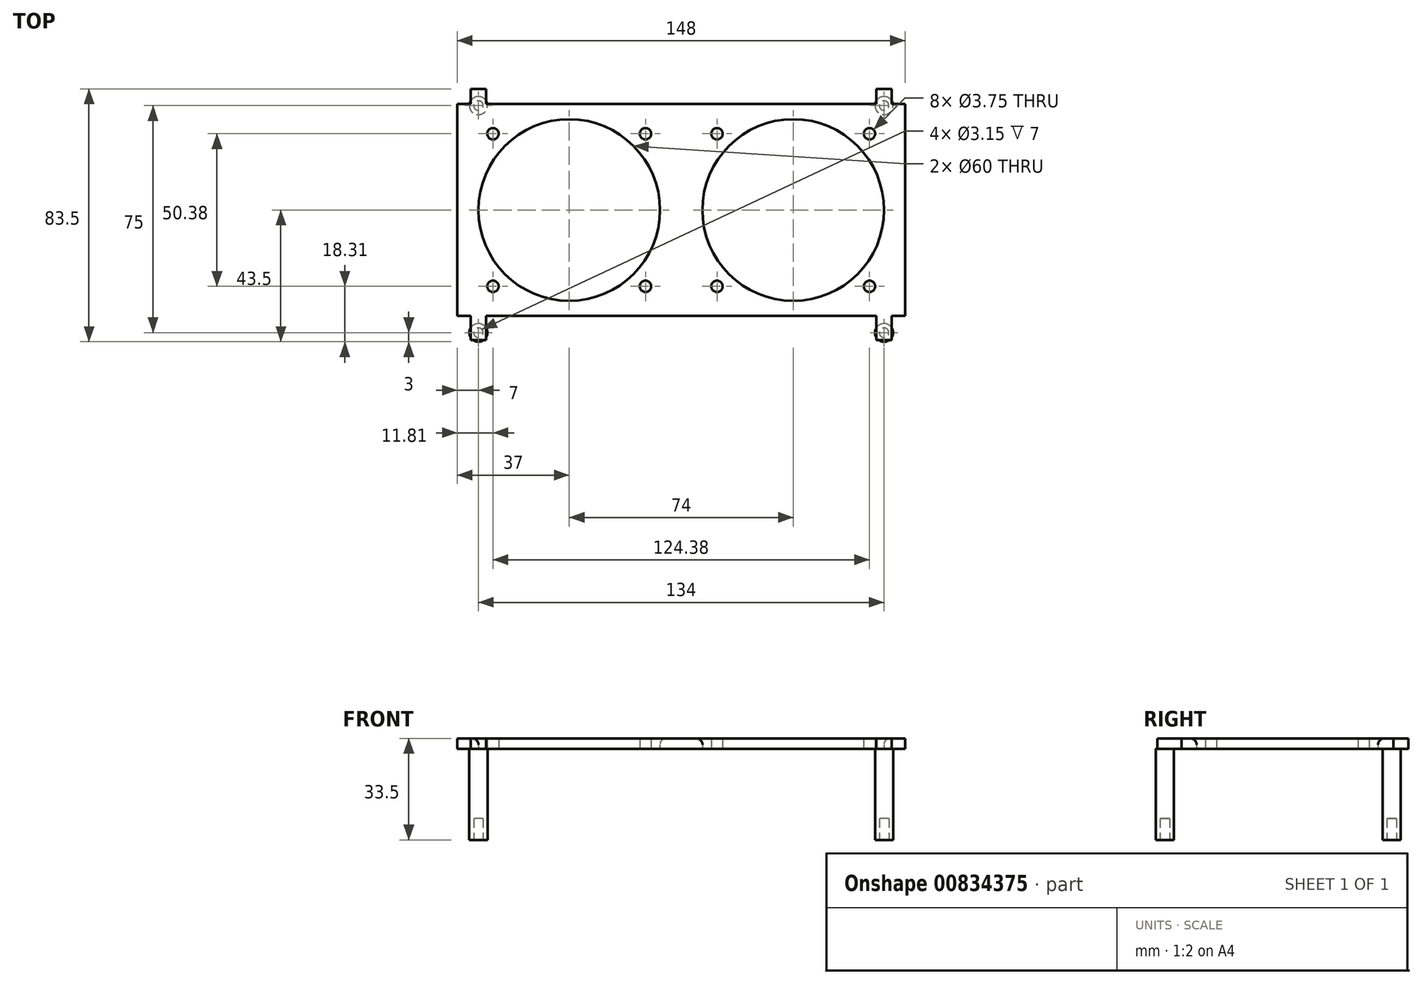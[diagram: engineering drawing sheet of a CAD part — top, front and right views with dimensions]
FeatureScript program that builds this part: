
annotation { "Feature Type Name" : "Feature", "Feature Type Description" : "" }
export const myFeature = defineFeature(function(context is Context, id is Id, definition is map)
    precondition{}
    {
        {
            var Q0;
            Q0=qCreatedBy(makeId("Top.planeOp"),FACE);
            var sketch = newSketch(context, id + "F0", { "sketchPlane" : qUnion([Q0])});
            skLineSegment(sketch, "E0.bottom", {"start": v(74, -35) * mm, "end": v(69.5, -35) * mm});
            skLineSegment(sketch, "E0.top", {"start": v(74, 35) * mm, "end": v(-74, 35) * mm});
            skLineSegment(sketch, "E0.left", {"start": v(74, -35) * mm, "end": v(74, 35) * mm});
            skLineSegment(sketch, "E0.right", {"start": v(-74, -35) * mm, "end": v(-74, 35) * mm});
            skPoint(sketch, "E0.middle", {"position": v(0, 0) * mm});
            skCircle(sketch, "E1", {"center": v(-37, 0) * mm, "radius": 30 * mm});
            skCircle(sketch, "E2", {"center": v(37, 0) * mm, "radius": 30 * mm});
            skLineSegment(sketch, "E3.bottom", {"start": v(-64.5, -43) * mm, "end": v(-69.5, -43) * mm});
            skLineSegment(sketch, "E3.left", {"start": v(-64.5, -43) * mm, "end": v(-64.5, -35) * mm});
            skLineSegment(sketch, "E3.right", {"start": v(-69.5, -43) * mm, "end": v(-69.5, -35) * mm});
            skPoint(sketch, "E3.middle", {"position": v(-67, -39) * mm});
            skLineSegment(sketch, "E4.bottom", {"start": v(69.5, -43) * mm, "end": v(64.5, -43) * mm});
            skLineSegment(sketch, "E4.left", {"start": v(69.5, -43) * mm, "end": v(69.5, -35) * mm});
            skLineSegment(sketch, "E4.right", {"start": v(64.5, -43) * mm, "end": v(64.5, -35) * mm});
            skPoint(sketch, "E4.middle", {"position": v(67, -39) * mm});
            skLineSegment(sketch, "E5.trimOffspring", {"start": v(-69.5, -35) * mm, "end": v(-74, -35) * mm});
            skLineSegment(sketch, "E6.trimOffspring", {"start": v(64.5, -35) * mm, "end": v(-64.5, -35) * mm});
            skLineSegment(sketch, "E7.bottom", {"start": v(-64.5, 35) * mm, "end": v(-69.5, 35) * mm});
            skLineSegment(sketch, "E7.top", {"start": v(-64.5, 40) * mm, "end": v(-69.5, 40) * mm});
            skLineSegment(sketch, "E7.left", {"start": v(-64.5, 35) * mm, "end": v(-64.5, 40) * mm});
            skLineSegment(sketch, "E7.right", {"start": v(-69.5, 35) * mm, "end": v(-69.5, 40) * mm});
            skPoint(sketch, "E7.middle", {"position": v(-67, 37.5) * mm});
            skLineSegment(sketch, "E8.bottom", {"start": v(69.5, 35) * mm, "end": v(64.5, 35) * mm});
            skLineSegment(sketch, "E8.top", {"start": v(69.5, 40) * mm, "end": v(64.5, 40) * mm});
            skLineSegment(sketch, "E8.left", {"start": v(69.5, 35) * mm, "end": v(69.5, 40) * mm});
            skLineSegment(sketch, "E8.right", {"start": v(64.5, 35) * mm, "end": v(64.5, 40) * mm});
            skPoint(sketch, "E8.middle", {"position": v(67, 37.5) * mm});
            skSolve(sketch);
        }
        {
            var Q0;
            Q0=makeQuery(id+"F0.imprint","IMPRINT",FACE,{"disambiguationData":[TD([[makeQuery(id+"F0.imprint","IMPRINT",EDGE,{"derivedFrom":sQuery(id+"F0.wireOp",EDGE,"E0.bottom")}),-1.0]])]});
            var sketch = newSketch(context, id + "F1", { "sketchPlane" : qUnion([Q0])});
            skCircle(sketch, "E9", {"center": v(-62.19, 25.2) * mm, "radius": 1.88 * mm});
            skCircle(sketch, "E10", {"center": v(-11.8, 25.19) * mm, "radius": 1.88 * mm});
            skCircle(sketch, "E11", {"center": v(-62.2, -25.19) * mm, "radius": 1.88 * mm});
            skCircle(sketch, "E12", {"center": v(-11.81, -25.2) * mm, "radius": 1.88 * mm});
            skLineSegment(sketch, "E13", {"start": v(-101.39, 0) * mm, "end": v(88.94, 0) * mm, "construction": true});
            skLineSegment(sketch, "E14", {"start": v(37, -51.4) * mm, "end": v(37, 53.55) * mm, "construction": true});
            skLineSegment(sketch, "E15", {"start": v(-37, 53.9) * mm, "end": v(-37, -62.16) * mm, "construction": true});
            skSolve(sketch);
        }
        {
            var Q0;
            Q0=qCreatedBy(makeId("Top.planeOp"),FACE);
            var sketch = newSketch(context, id + "F2", { "sketchPlane" : qUnion([Q0])});
            skCircle(sketch, "E16", {"center": v(11.8, 25.2) * mm, "radius": 1.88 * mm});
            skCircle(sketch, "E17", {"center": v(11.8, -25.2) * mm, "radius": 1.88 * mm});
            skCircle(sketch, "E18", {"center": v(62.19, 25.19) * mm, "radius": 1.88 * mm});
            skCircle(sketch, "E19", {"center": v(62.19, -25.2) * mm, "radius": 1.88 * mm});
            skSolve(sketch);
        }
        {
            var Q0;
            Q0 = qSketchRegion(id + "F0", true);
            extrude(context, id + "F3", {"entities" : qUnion([Q0]), "depth" : 3.5 * mm, "offsetDistance" : 25 * mm});
        }
        {
            var Q0;
            Q0 = qSketchRegion(id + "F1", true);
            extrude(context, id + "F4", {"entities" : qUnion([Q0]), "operationType" : NewBodyOperationType.REMOVE, "depth" : 25 * mm, "offsetDistance" : 25 * mm});
        }
        {
            var Q0;
            Q0 = qSketchRegion(id + "F2", true);
            extrude(context, id + "F5", {"entities" : qUnion([Q0]), "operationType" : NewBodyOperationType.REMOVE, "depth" : 25 * mm, "offsetDistance" : 25 * mm});
        }
        {
            var Q0;
            Q0=makeQuery(id+"F3.opExtrude","CAP_EDGE",EDGE,{"disambiguationData":[OSD([sQuery(id+"F0.wireOp",EDGE,"E1")])],"isStart":false});
            var Q1;
            Q1=makeQuery(id+"F3.opExtrude","CAP_EDGE",EDGE,{"disambiguationData":[OSD([sQuery(id+"F0.wireOp",EDGE,"E2")])],"isStart":false});
            fillet(context, id + "F6", {"entities" : qUnion([Q0, Q1]), "radius" : 2 * mm, "tangentPropagation" : true, "allowEdgeOverflow" : false});
        }
        {
            var Q0;
            Q0=qCreatedBy(makeId("Top.planeOp"),FACE);
            var sketch = newSketch(context, id + "F7", { "sketchPlane" : qUnion([Q0])});
            skCircle(sketch, "E20", {"center": v(-67, -40.5) * mm, "radius": 3 * mm});
            skCircle(sketch, "E21", {"center": v(67, -40.5) * mm, "radius": 3 * mm});
            skCircle(sketch, "E22", {"center": v(-67, 34.5) * mm, "radius": 3 * mm});
            skCircle(sketch, "E23", {"center": v(67, 34.5) * mm, "radius": 3 * mm});
            skSolve(sketch);
        }
        {
            var Q0;
            Q0 = qSketchRegion(id + "F7", true);
            extrude(context, id + "F8", {"entities" : qUnion([Q0]), "operationType" : NewBodyOperationType.ADD, "oppositeDirection" : true, "depth" : 30 * mm, "offsetDistance" : 25 * mm});
        }
        {
            var Q0;
            Q0=qCreatedBy(makeId("Top.planeOp"),FACE);
            cPlane(context, id + "F9", {"entities" : qUnion([Q0]), "cplaneType" : CPlaneType.OFFSET, "offset" : 30 * mm, "oppositeDirection" : true, "width" : 150 * mm, "height" : 150 * mm});
        }
        {
            var Q0;
            Q0=qCreatedBy(id+"F9.planeOp",FACE);
            var sketch = newSketch(context, id + "F10", { "sketchPlane" : qUnion([Q0])});
            skCircle(sketch, "E24", {"center": v(-67, -40.5) * mm, "radius": 1.57 * mm});
            skCircle(sketch, "E25", {"center": v(-67, 34.5) * mm, "radius": 1.57 * mm});
            skCircle(sketch, "E26", {"center": v(67, -40.5) * mm, "radius": 1.57 * mm});
            skCircle(sketch, "E27", {"center": v(67, 34.5) * mm, "radius": 1.57 * mm});
            skSolve(sketch);
        }
        {
            var Q0;
            Q0 = qSketchRegion(id + "F10", true);
            extrude(context, id + "F11", {"entities" : qUnion([Q0]), "operationType" : NewBodyOperationType.REMOVE, "depth" : 7 * mm, "offsetDistance" : 25 * mm});
        }
    });
